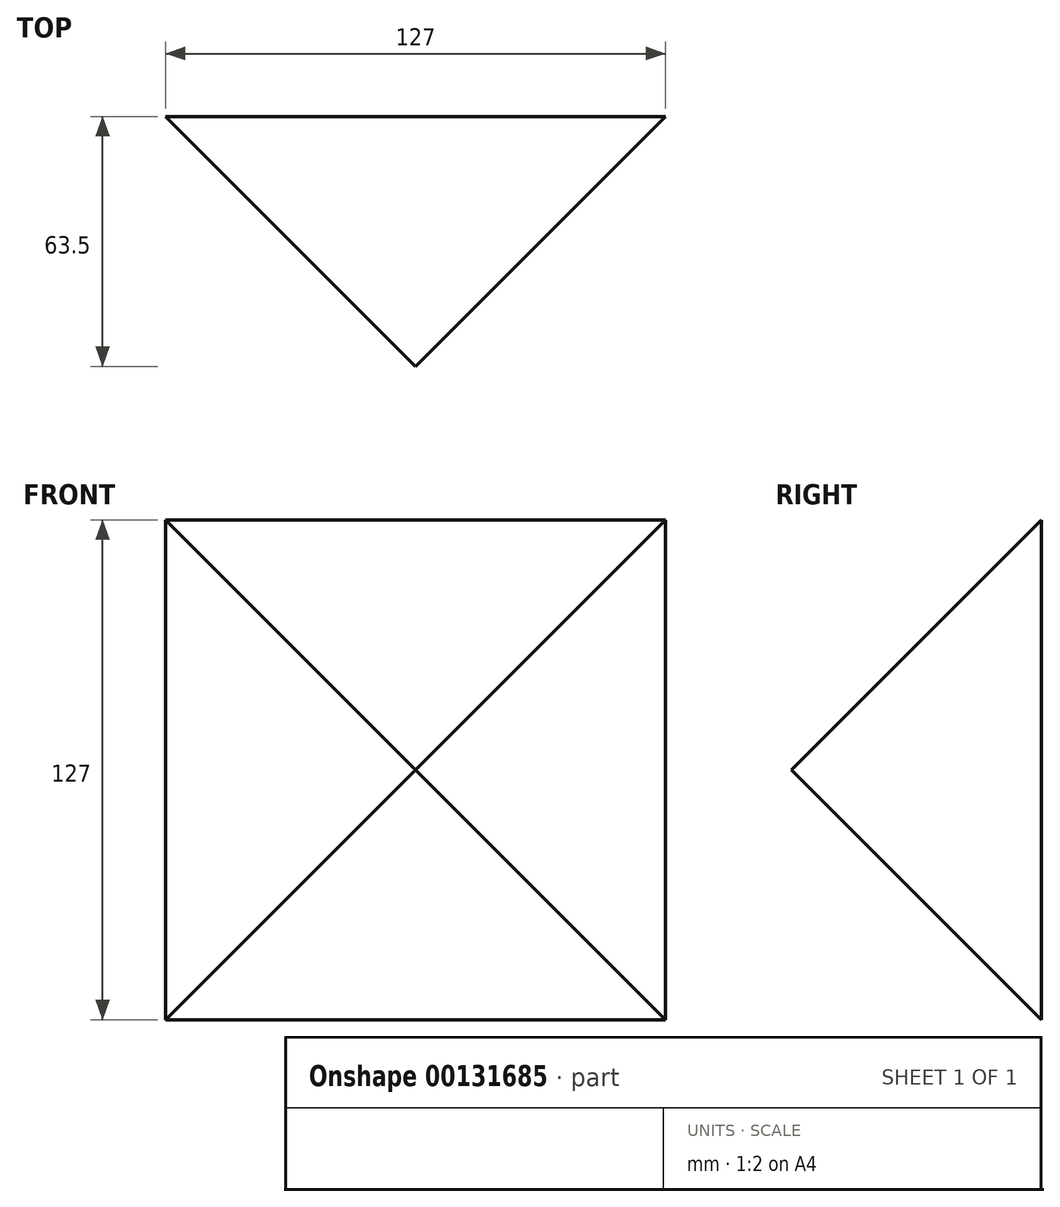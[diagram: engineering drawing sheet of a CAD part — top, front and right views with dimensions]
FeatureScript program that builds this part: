
annotation { "Feature Type Name" : "Feature", "Feature Type Description" : "" }
export const myFeature = defineFeature(function(context is Context, id is Id, definition is map)
    precondition{}
    {
        {
            var Q0;
            Q0=qCreatedBy(makeId("Front.planeOp"),FACE);
            var sketch = newSketch(context, id + "F0", { "sketchPlane" : qUnion([Q0])});
            skLineSegment(sketch, "E0.bottom", {"start": v(-63.5, 63.5) * mm, "end": v(63.5, 63.5) * mm});
            skLineSegment(sketch, "E0.top", {"start": v(-63.5, -63.5) * mm, "end": v(63.5, -63.5) * mm});
            skLineSegment(sketch, "E0.left", {"start": v(-63.5, 63.5) * mm, "end": v(-63.5, -63.5) * mm});
            skLineSegment(sketch, "E0.right", {"start": v(63.5, 63.5) * mm, "end": v(63.5, -63.5) * mm});
            skPoint(sketch, "E0.middle", {"position": v(0, 0) * mm});
            skSolve(sketch);
        }
        {
            var Q0;
            Q0 = qSketchRegion(id + "F0", true);
            extrude(context, id + "F1", {"entities" : qUnion([Q0]), "depth" : 254 * mm, "hasDraft" : true, "draftAngle" : 45 * degree, "draftPullDirection" : true});
        }
    });
